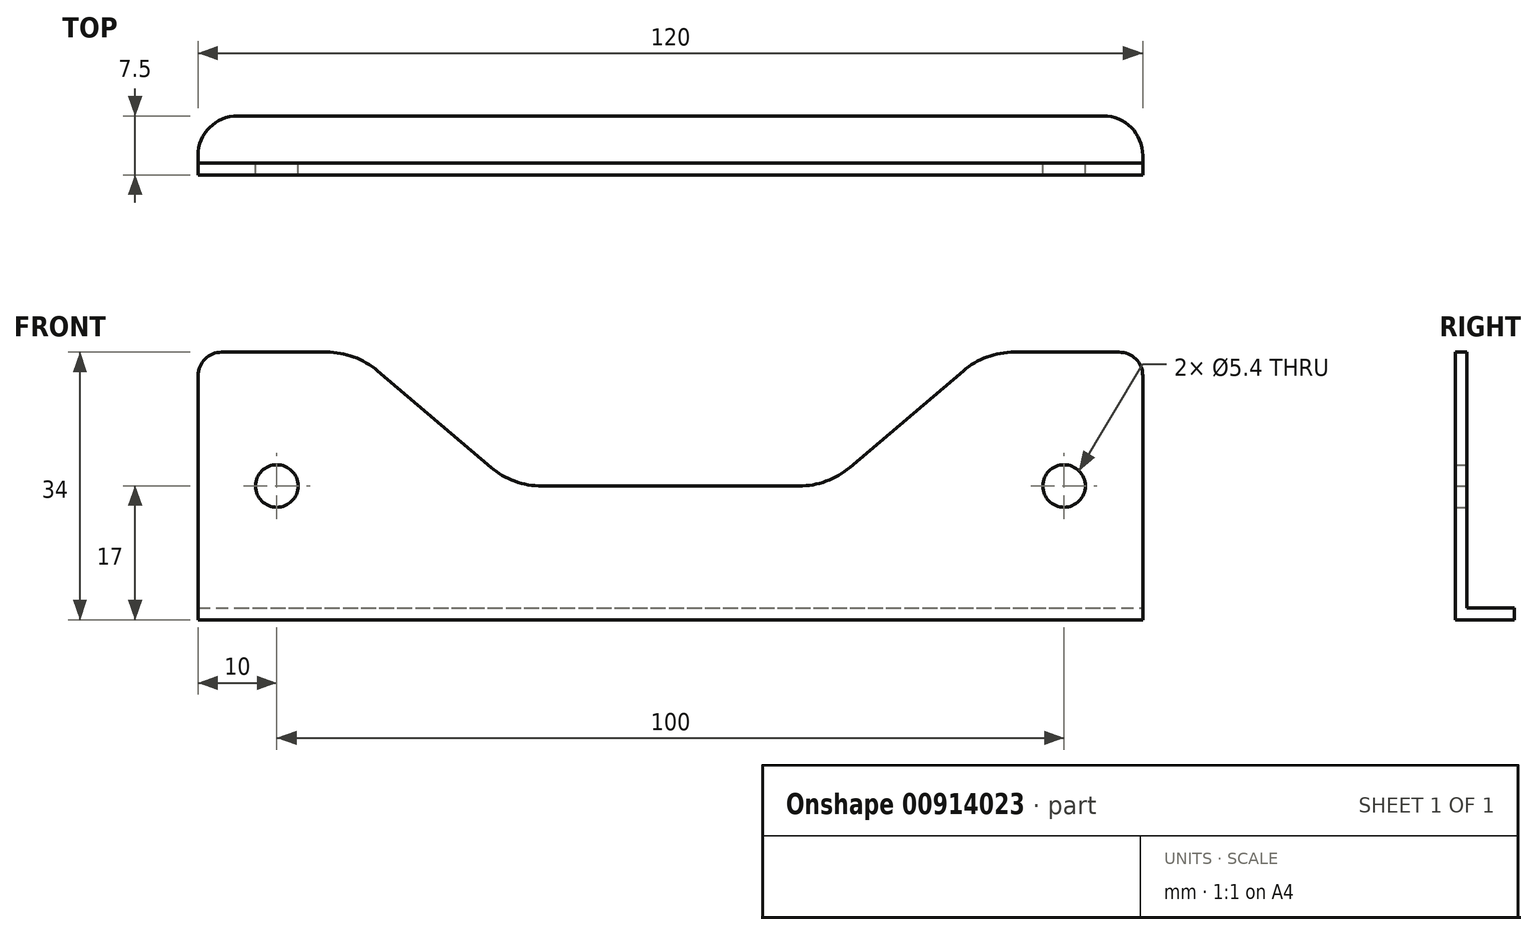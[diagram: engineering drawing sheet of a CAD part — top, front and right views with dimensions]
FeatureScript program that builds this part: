
annotation { "Feature Type Name" : "Feature", "Feature Type Description" : "" }
export const myFeature = defineFeature(function(context is Context, id is Id, definition is map)
    precondition{}
    {
        {
            var Q0;
            Q0=qCreatedBy(makeId("Front.planeOp"),FACE);
            var sketch = newSketch(context, id + "F0", { "sketchPlane" : qUnion([Q0])});
            skCircle(sketch, "E0", {"center": v(0, 0) * mm, "radius": 95 * mm});
            skCircle(sketch, "E1", {"center": v(0, 0) * mm, "radius": 45 * mm});
            skCircle(sketch, "E2", {"center": v(-50, -85) * mm, "radius": 2.7 * mm});
            skCircle(sketch, "E3.MirrorC", {"center": v(50, -85) * mm, "radius": 2.7 * mm});
            skLineSegment(sketch, "E4.bottom", {"start": v(-60, -102) * mm, "end": v(60, -102) * mm});
            skLineSegment(sketch, "E4.top", {"start": v(-57, -68) * mm, "end": v(-43.68, -68) * mm});
            skLineSegment(sketch, "E4.left", {"start": v(-60, -102) * mm, "end": v(-60, -71) * mm});
            skLineSegment(sketch, "E4.right", {"start": v(60, -102) * mm, "end": v(60, -71) * mm});
            skPoint(sketch, "E4.middle", {"position": v(0, -85) * mm});
            skLineSegment(sketch, "E5", {"start": v(-37.2, -70.38) * mm, "end": v(-22.8, -82.62) * mm});
            skLineSegment(sketch, "E6", {"start": v(-16.32, -85) * mm, "end": v(0, -85) * mm});
            skLineSegment(sketch, "E7", {"start": v(0, -85) * mm, "end": v(16.32, -85) * mm});
            skLineSegment(sketch, "E8", {"start": v(22.8, -82.62) * mm, "end": v(37.2, -70.38) * mm});
            skLineSegment(sketch, "E9.trimOffspring", {"start": v(43.68, -68) * mm, "end": v(57, -68) * mm});
            skPoint(sketch, "E10.visualSharp", {"position": v(-60, -68) * mm});
            skArc(sketch, "E10.filletArc", {"start": v(-57, -68) * mm, "mid": v(-59.12, -68.88) * mm, "end": v(-60, -71) * mm});
            skPoint(sketch, "E11.visualSharp", {"position": v(-60, -102) * mm});
            skLineSegment(sketch, "E11.filletArc", {"start": v(-60, -102) * mm, "end": v(-60, -102) * mm});
            skPoint(sketch, "E12.visualSharp", {"position": v(-40, -68) * mm});
            skArc(sketch, "E12.filletArc", {"start": v(-37.2, -70.38) * mm, "mid": v(-40.23, -68.61) * mm, "end": v(-43.68, -68) * mm});
            skPoint(sketch, "E13.visualSharp", {"position": v(-20, -85) * mm});
            skArc(sketch, "E13.filletArc", {"start": v(-22.8, -82.62) * mm, "mid": v(-19.77, -84.39) * mm, "end": v(-16.32, -85) * mm});
            skPoint(sketch, "E14.visualSharp", {"position": v(20, -85) * mm});
            skArc(sketch, "E14.filletArc", {"start": v(16.32, -85) * mm, "mid": v(19.77, -84.39) * mm, "end": v(22.8, -82.62) * mm});
            skPoint(sketch, "E15.visualSharp", {"position": v(40, -68) * mm});
            skArc(sketch, "E15.filletArc", {"start": v(43.68, -68) * mm, "mid": v(40.23, -68.61) * mm, "end": v(37.2, -70.38) * mm});
            skPoint(sketch, "E16.visualSharp", {"position": v(60, -68) * mm});
            skArc(sketch, "E16.filletArc", {"start": v(60, -71) * mm, "mid": v(59.12, -68.88) * mm, "end": v(57, -68) * mm});
            skSolve(sketch);
        }
        {
            var Q0;
            {var subQ1=sQuery(id+"F0.wireOp",EDGE,"E4.top");Q0=makeQuery(id+"F0.imprint","IMPRINT",FACE,{"disambiguationData":[TD([[makeQuery(id+"F0.imprint","IMPRINT",EDGE,{"derivedFrom":subQ1}),-1.0]])]});}
            var Q1;
            Q1=makeQuery(id+"F0.imprint","IMPRINT",FACE,{"disambiguationData":[TD([[makeQuery(id+"F0.imprint","IMPRINT",EDGE,{"derivedFrom":sQuery(id+"F0.wireOp",EDGE,"E2")}),-1.0]])]});
            extrude(context, id + "F1", {"entities" : qUnion([Q0, Q1]), "depth" : 1.5 * mm, "offsetDistance" : 25 * mm});
        }
        {
            var Q0;
            Q0=makeQuery(id+"F1.opExtrude","CAP_FACE",FACE,{"disambiguationData":[OSD([sQuery(id+"F0.wireOp",EDGE,"E2"),sQuery(id+"F0.wireOp",EDGE,"E3.MirrorC"),sQuery(id+"F0.wireOp",EDGE,"E4.bottom"),sQuery(id+"F0.wireOp",EDGE,"E4.top"),sQuery(id+"F0.wireOp",EDGE,"E4.left"),sQuery(id+"F0.wireOp",EDGE,"E4.right"),sQuery(id+"F0.wireOp",EDGE,"E5"),sQuery(id+"F0.wireOp",EDGE,"E6"),sQuery(id+"F0.wireOp",EDGE,"E7"),sQuery(id+"F0.wireOp",EDGE,"E8"),sQuery(id+"F0.wireOp",EDGE,"E9.trimOffspring"),sQuery(id+"F0.wireOp",EDGE,"E10.filletArc"),sQuery(id+"F0.wireOp",EDGE,"E12.filletArc"),sQuery(id+"F0.wireOp",EDGE,"E13.filletArc"),sQuery(id+"F0.wireOp",EDGE,"E14.filletArc"),sQuery(id+"F0.wireOp",EDGE,"E15.filletArc"),sQuery(id+"F0.wireOp",EDGE,"E16.filletArc")])],"isStart":false});
            var sketch = newSketch(context, id + "F2", { "sketchPlane" : qUnion([Q0])});
            skLineSegment(sketch, "E17.bottom", {"start": v(-60, -102) * mm, "end": v(60, -102) * mm});
            skLineSegment(sketch, "E17.top", {"start": v(-60, -100.5) * mm, "end": v(60, -100.5) * mm});
            skLineSegment(sketch, "E17.left", {"start": v(-60, -102) * mm, "end": v(-60, -100.5) * mm});
            skLineSegment(sketch, "E17.right", {"start": v(60, -102) * mm, "end": v(60, -100.5) * mm});
            skSolve(sketch);
        }
        {
            var Q0;
            Q0 = qSketchRegion(id + "F2", true);
            extrude(context, id + "F3", {"entities" : qUnion([Q0]), "operationType" : NewBodyOperationType.ADD, "oppositeDirection" : true, "depth" : 7.5 * mm, "offsetDistance" : 25 * mm});
        }
        {
            var Q0;
            Q0=makeQuery(id+"F3.opExtrude","CAP_EDGE",EDGE,{"disambiguationData":[OSD([sQuery(id+"F2.wireOp",EDGE,"E17.right")])],"isStart":false});
            var Q1;
            Q1=makeQuery(id+"F3.opExtrude","CAP_EDGE",EDGE,{"disambiguationData":[OSD([sQuery(id+"F2.wireOp",EDGE,"E17.left")])],"isStart":false});
            fillet(context, id + "F4", {"entities" : qUnion([Q0, Q1]), "radius" : 5 * mm, "tangentPropagation" : true, "allowEdgeOverflow" : false});
        }
    });
